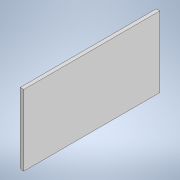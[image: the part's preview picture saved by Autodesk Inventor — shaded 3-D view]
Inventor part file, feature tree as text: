
AUTODESK INVENTOR PART (.ipt)
format: ipt  version: 2020 (Build 240168000, 168)  size: 88,576 bytes
history: native  units: mm
features: sketch x2, other x1, extrude x1
ambient origin geometry x8: Origin, YZ Plane, XZ Plane, XY Plane, X Axis, Y Axis, Z Axis, Center Point
bodies: Body1 (feature_tree)
feature tree (4):
  other  "Bryła1"
  sketch  "Szkic1"
  extrude  "Wyciągnięcie proste1"  Depth=300.0mm
  sketch  "Szkic2"
